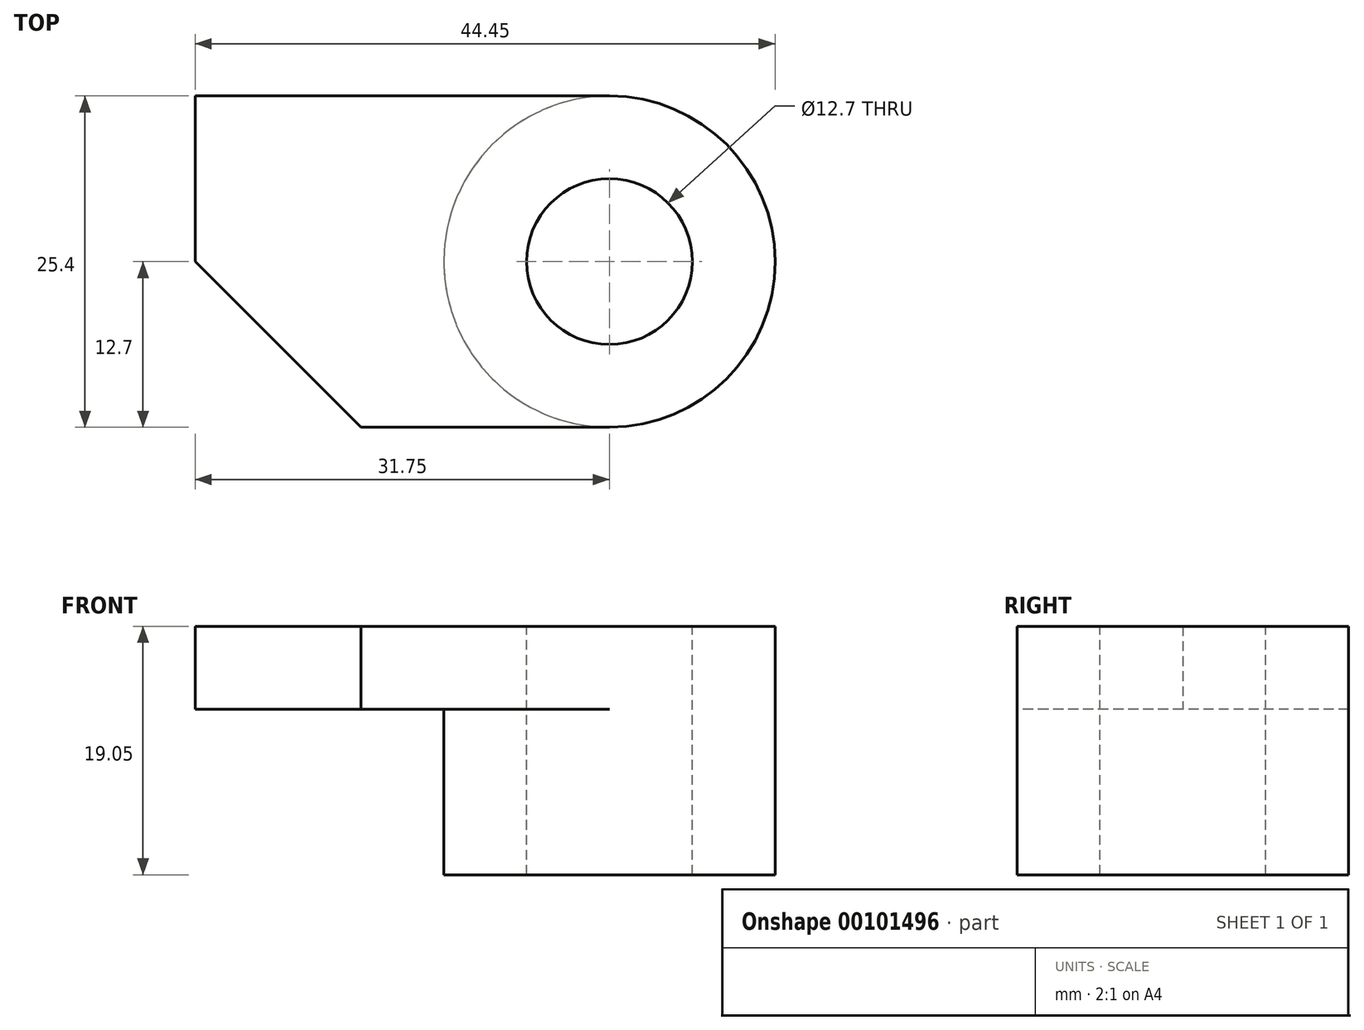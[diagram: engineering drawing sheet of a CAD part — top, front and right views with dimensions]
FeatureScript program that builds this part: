
annotation { "Feature Type Name" : "Feature", "Feature Type Description" : "" }
export const myFeature = defineFeature(function(context is Context, id is Id, definition is map)
    precondition{}
    {
        {
            var Q0;
            Q0=qCreatedBy(makeId("Top.planeOp"),FACE);
            var sketch = newSketch(context, id + "F0", { "sketchPlane" : qUnion([Q0])});
            skLineSegment(sketch, "E0", {"start": v(0, 0) * mm, "end": v(0, 25.4) * mm});
            skLineSegment(sketch, "E1", {"start": v(0, 25.4) * mm, "end": v(-31.75, 25.4) * mm});
            skLineSegment(sketch, "E2", {"start": v(-31.75, 25.4) * mm, "end": v(-31.75, 12.7) * mm});
            skLineSegment(sketch, "E3", {"start": v(-31.75, 12.7) * mm, "end": v(-19.05, 0) * mm});
            skLineSegment(sketch, "E4", {"start": v(-19.05, 0) * mm, "end": v(0, 0) * mm});
            skSolve(sketch);
        }
        {
            var Q0;
            Q0=makeQuery(id+"F0.imprint","IMPRINT",FACE,{"disambiguationData":[TD([[makeQuery(id+"F0.imprint","IMPRINT",EDGE,{"derivedFrom":sQuery(id+"F0.wireOp",EDGE,"E0")}),1.0]])]});
            extrude(context, id + "F1", {"entities" : qUnion([Q0]), "depth" : 6.35 * mm});
        }
        {
            var Q0;
            Q0=makeQuery(id+"F1.opExtrude","CAP_FACE",FACE,{"disambiguationData":[OSD([sQuery(id+"F0.wireOp",EDGE,"E0"),sQuery(id+"F0.wireOp",EDGE,"E1"),sQuery(id+"F0.wireOp",EDGE,"E2"),sQuery(id+"F0.wireOp",EDGE,"E3"),sQuery(id+"F0.wireOp",EDGE,"E4")])],"isStart":false});
            var sketch = newSketch(context, id + "F2", { "sketchPlane" : qUnion([Q0])});
            skCircle(sketch, "E5", {"center": v(0, 12.7) * mm, "radius": 12.7 * mm});
            skCircle(sketch, "E6", {"center": v(0, 12.7) * mm, "radius": 6.35 * mm});
            skSolve(sketch);
        }
        {
            var Q0;
            {var subQ1=makeQuery(id+"F1.opExtrude","CAP_EDGE",EDGE,{"disambiguationData":[OSD([sQuery(id+"F0.wireOp",EDGE,"E0")])],"isStart":false});var subQ4=sQuery(id+"F2.wireOp",EDGE,"E6");var subQ5=makeQuery(id+"F2.imprint","INTERSECT",VERTEX,{"disambiguationData":[OD(0.0)],"derivedFrom":[subQ1,subQ4]});Q0=makeQuery(id+"F2.imprint","IMPRINT",FACE,{"disambiguationData":[TD([[makeQuery(id+"F2.imprint","IMPRINT",EDGE,{"disambiguationData":[TD([[subQ5,-1.0]])],"derivedFrom":subQ4}),-1.0]])]});}
            var Q1;
            {var subQ1=makeQuery(id+"F1.opExtrude","CAP_EDGE",EDGE,{"disambiguationData":[OSD([sQuery(id+"F0.wireOp",EDGE,"E0")])],"isStart":false});var subQ4=sQuery(id+"F2.wireOp",EDGE,"E6");var subQ5=makeQuery(id+"F2.imprint","INTERSECT",VERTEX,{"disambiguationData":[OD(0.0)],"derivedFrom":[subQ1,subQ4]});Q1=makeQuery(id+"F2.imprint","IMPRINT",FACE,{"disambiguationData":[TD([[makeQuery(id+"F2.imprint","IMPRINT",EDGE,{"disambiguationData":[TD([[subQ5,1.0]])],"derivedFrom":subQ4}),-1.0]])]});}
            extrude(context, id + "F3", {"entities" : qUnion([Q0, Q1]), "operationType" : NewBodyOperationType.ADD, "oppositeDirection" : true, "depth" : 19.05 * mm});
        }
        {
            var Q0;
            {var subQ0=sQuery(id+"F0.wireOp",EDGE,"E0");Q0=makeQuery(id+"F3.boolean.opBoolean","SPLIT",FACE,{"disambiguationData":[TD([makeQuery(id+"F1.opExtrude","SWEPT_FACE",FACE,{"disambiguationData":[OSD([subQ0])]})])],"derivedFrom":makeQuery(id+"F1.opExtrude","CAP_FACE",FACE,{"disambiguationData":[OSD([subQ0,sQuery(id+"F0.wireOp",EDGE,"E1"),sQuery(id+"F0.wireOp",EDGE,"E2"),sQuery(id+"F0.wireOp",EDGE,"E3"),sQuery(id+"F0.wireOp",EDGE,"E4")])],"isStart":true})});}
            extrude(context, id + "F4", {"entities" : qUnion([Q0]), "operationType" : NewBodyOperationType.REMOVE, "endBound" : BoundingType.THROUGH_ALL, "oppositeDirection" : true, "depth" : 25.4 * mm});
        }
    });
